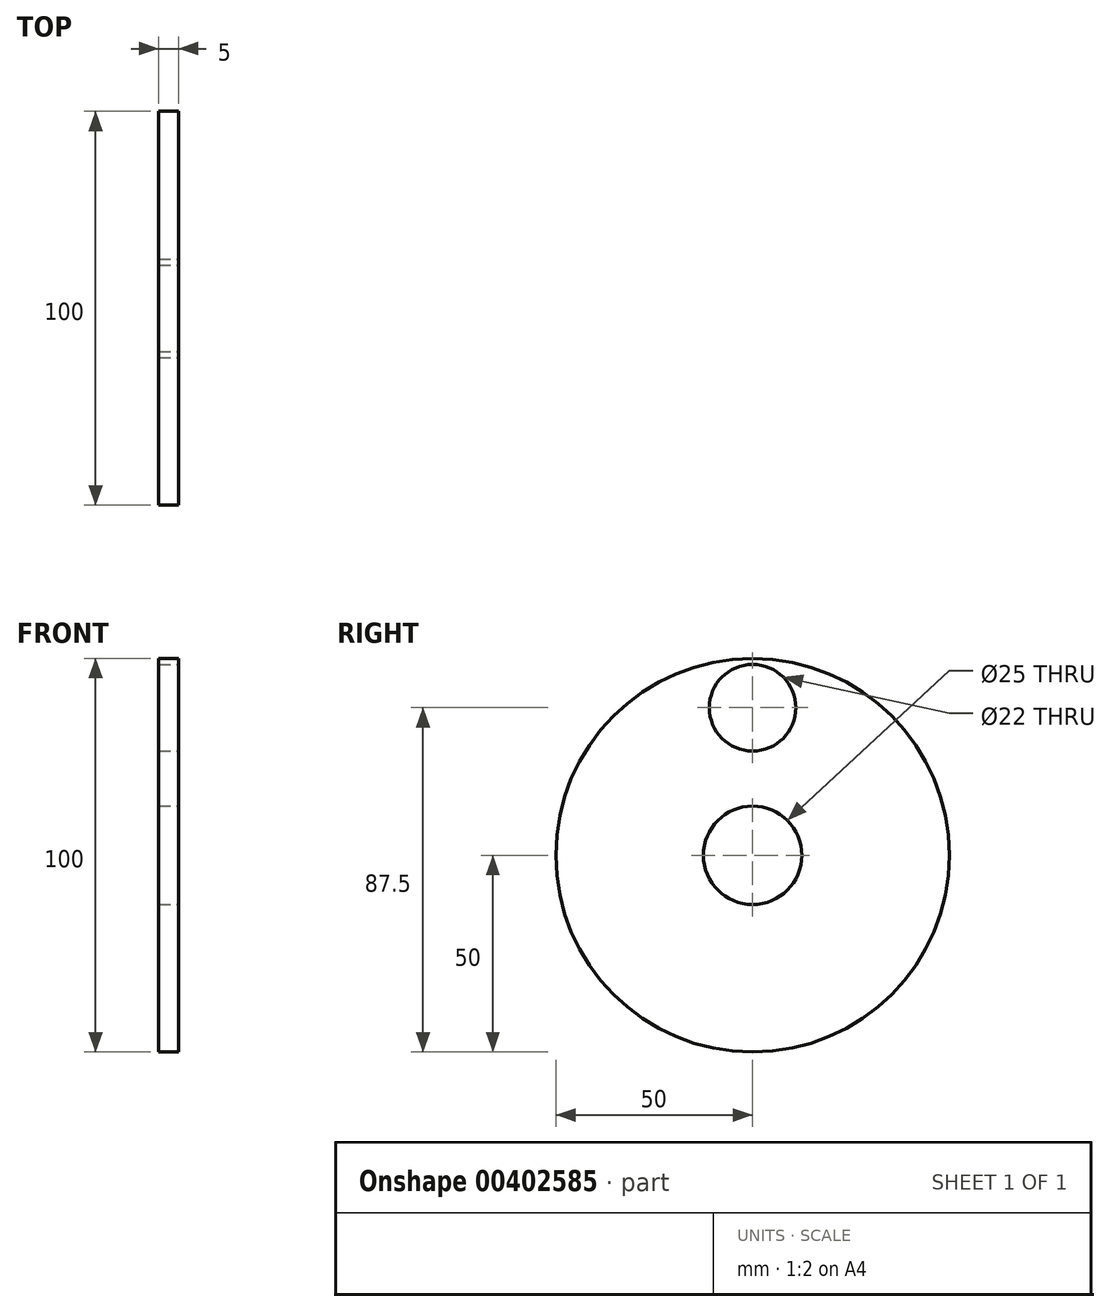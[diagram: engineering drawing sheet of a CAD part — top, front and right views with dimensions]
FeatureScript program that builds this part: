
annotation { "Feature Type Name" : "Feature", "Feature Type Description" : "" }
export const myFeature = defineFeature(function(context is Context, id is Id, definition is map)
    precondition{}
    {
        {
            var Q0;
            Q0=qCreatedBy(makeId("Right.planeOp"),FACE);
            var sketch = newSketch(context, id + "F0", { "sketchPlane" : qUnion([Q0])});
            skCircle(sketch, "E0", {"center": v(0, 0) * mm, "radius": 50 * mm});
            skSolve(sketch);
        }
        {
            var Q0;
            Q0 = qSketchRegion(id + "F0", true);
            extrude(context, id + "F1", {"entities" : qUnion([Q0]), "endBound" : BoundingType.SYMMETRIC, "depth" : 5 * mm});
        }
        {
            var Q0;
            Q0=makeQuery(id+"F1.opExtrude","CAP_FACE",FACE,{"disambiguationData":[OSD([sQuery(id+"F0.wireOp",EDGE,"E0")])],"isStart":false});
            var sketch = newSketch(context, id + "F2", { "sketchPlane" : qUnion([Q0])});
            skPoint(sketch, "E1", {"position": v(0, 0) * mm});
            skSolve(sketch);
        }
        {
            var Q0;
            Q0=sQuery(id+"F2.wireOp",VERTEX,"E1");
            var Q1;
            Q1=makeQuery(id+"F1.opExtrude","SWEPT_BODY",BODY,{"disambiguationData":[OSD([sQuery(id+"F0.wireOp",EDGE,"E0")])]});
            hole(context, id + "F3", {"style" : HoleStyle.SIMPLE, "endStyle" : HoleEndStyle.THROUGH, "holeDiameter" : 25 * mm, "isTappedThrough" : true, "tappedDepth" : 12 * mm, "tapClearance" : 3, "locations" : qUnion([Q0]), "scope" : qUnion([Q1])});
        }
        {
            var Q0;
            Q0=makeQuery(id+"F1.opExtrude","CAP_FACE",FACE,{"disambiguationData":[OSD([sQuery(id+"F0.wireOp",EDGE,"E0")])],"isStart":false});
            var sketch = newSketch(context, id + "F4", { "sketchPlane" : qUnion([Q0])});
            skCircle(sketch, "E2", {"center": v(0, 0) * mm, "radius": 25 * mm, "construction": true});
            skCircle(sketch, "E3.0", {"center": v(0, 0) * mm, "radius": 50 * mm, "construction": true});
            skLineSegment(sketch, "E4", {"start": v(0, 50) * mm, "end": v(0, 25) * mm, "construction": true});
            skPoint(sketch, "E5", {"position": v(0, 37.5) * mm});
            skSolve(sketch);
        }
        {
            var Q0;
            Q0=sQuery(id+"F4.wireOp",VERTEX,"E5");
            var Q1;
            Q1=makeQuery(id+"F1.opExtrude","SWEPT_BODY",BODY,{"disambiguationData":[OSD([sQuery(id+"F0.wireOp",EDGE,"E0")])]});
            hole(context, id + "F5", {"style" : HoleStyle.SIMPLE, "endStyle" : HoleEndStyle.THROUGH, "holeDiameter" : 22 * mm, "isTappedThrough" : true, "tappedDepth" : 12 * mm, "tapClearance" : 3, "locations" : qUnion([Q0]), "scope" : qUnion([Q1])});
        }
    });
